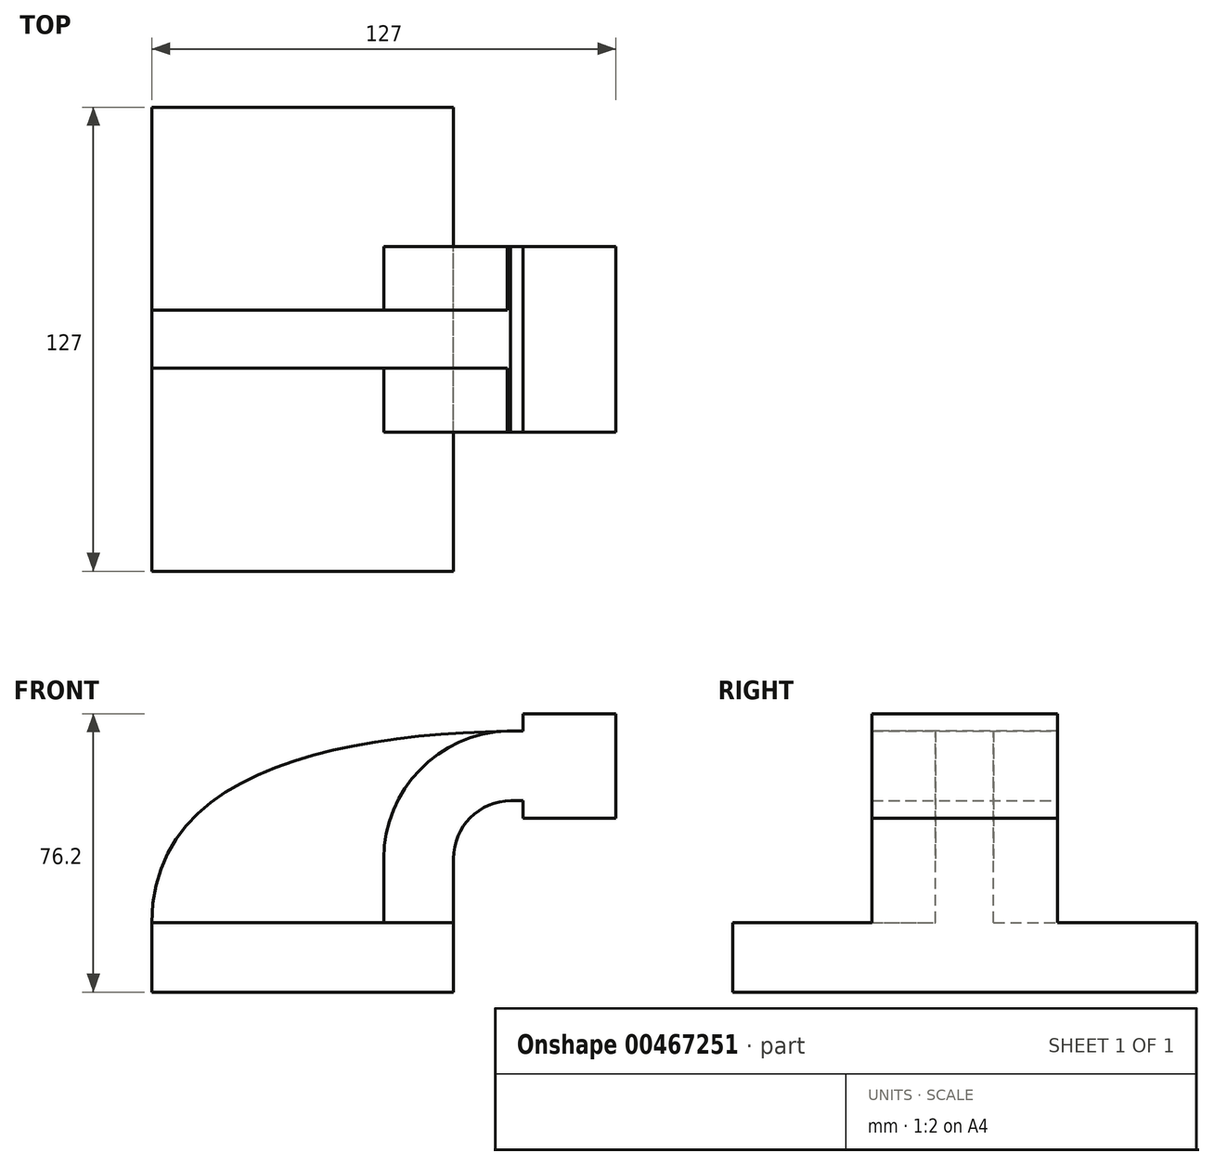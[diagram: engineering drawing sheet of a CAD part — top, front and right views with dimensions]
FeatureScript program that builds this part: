
annotation { "Feature Type Name" : "Feature", "Feature Type Description" : "" }
export const myFeature = defineFeature(function(context is Context, id is Id, definition is map)
    precondition{}
    {
        {
            var Q0;
            Q0=qCreatedBy(makeId("Front.planeOp"),FACE);
            var sketch = newSketch(context, id + "F0", { "sketchPlane" : qUnion([Q0])});
            skLineSegment(sketch, "E0.bottom", {"start": v(41.27, 9.53) * mm, "end": v(-41.28, 9.53) * mm});
            skLineSegment(sketch, "E0.top", {"start": v(41.28, -9.52) * mm, "end": v(-41.27, -9.53) * mm});
            skLineSegment(sketch, "E0.left", {"start": v(41.28, 9.53) * mm, "end": v(41.28, -9.52) * mm});
            skLineSegment(sketch, "E0.right", {"start": v(-41.28, 9.53) * mm, "end": v(-41.27, -9.52) * mm});
            skPoint(sketch, "E0.middle", {"position": v(0, 0) * mm});
            skLineSegment(sketch, "E1.bottom", {"start": v(111.13, 66.68) * mm, "end": v(60.33, 66.68) * mm});
            skLineSegment(sketch, "E1.top", {"start": v(111.13, 38.1) * mm, "end": v(60.33, 38.1) * mm});
            skLineSegment(sketch, "E1.left", {"start": v(111.13, 66.68) * mm, "end": v(111.13, 38.1) * mm});
            skLineSegment(sketch, "E1.right", {"start": v(60.32, 66.68) * mm, "end": v(60.33, 38.1) * mm});
            skPoint(sketch, "E1.middle", {"position": v(85.73, 52.39) * mm});
            skLineSegment(sketch, "E2", {"start": v(41.27, 9.53) * mm, "end": v(41.27, 27) * mm});
            skArc(sketch, "E3", {"start": v(41.28, 27) * mm, "mid": v(45.89, 38.19) * mm, "end": v(57.04, 42.88) * mm});
            skLineSegment(sketch, "E4", {"start": v(57.04, 42.88) * mm, "end": v(60.33, 42.88) * mm});
            skLineSegment(sketch, "E5", {"start": v(57.04, 42.88) * mm, "end": v(85.62, 43.07) * mm});
            skLineSegment(sketch, "E6.0", {"start": v(56.91, 61.92) * mm, "end": v(85.5, 62.12) * mm});
            skArc(sketch, "E6.1", {"start": v(22.23, 27) * mm, "mid": v(32.37, 51.61) * mm, "end": v(56.91, 61.92) * mm});
            skLineSegment(sketch, "E6.2", {"start": v(22.22, 9.53) * mm, "end": v(22.22, 27) * mm});
            skLineSegment(sketch, "E7", {"start": v(85.73, 38.1) * mm, "end": v(85.73, 66.68) * mm});
            skFitSpline(sketch, "E8", {"points": [v(-41.28, 9.53) * mm, v(56.91, 61.92) * mm], "startDerivative": vector(0.02, 125.3) * mm, "endDerivative": vector(139.57, 2.52) * mm});
            skSolve(sketch);
        }
        {
            var Q0;
            Q0=makeQuery(id+"F0.imprint","IMPRINT",FACE,{"disambiguationData":[TD([[makeQuery(id+"F0.imprint","IMPRINT",EDGE,{"derivedFrom":sQuery(id+"F0.wireOp",EDGE,"E0.top")}),-1.0]])]});
            extrude(context, id + "F1", {"entities" : qUnion([Q0]), "endBound" : BoundingType.SYMMETRIC, "depth" : 127 * mm});
        }
        {
            var Q0;
            {var subQ0=sQuery(id+"F0.wireOp",EDGE,"E2");Q0=makeQuery(id+"F0.imprint","IMPRINT",FACE,{"disambiguationData":[TD([[makeQuery(id+"F0.imprint","IMPRINT",EDGE,{"derivedFrom":subQ0}),1.0]])]});}
            var Q1;
            {var subQ6=sQuery(id+"F0.wireOp",EDGE,"E7");Q1=makeQuery(id+"F0.imprint","IMPRINT",FACE,{"disambiguationData":[TD([[makeQuery(id+"F0.imprint","IMPRINT",EDGE,{"derivedFrom":subQ6}),1.0]])]});}
            extrude(context, id + "F2", {"entities" : qUnion([Q0, Q1]), "operationType" : NewBodyOperationType.ADD, "endBound" : BoundingType.SYMMETRIC, "depth" : 50.8 * mm});
        }
        {
            var Q0;
            {var subQ3=sQuery(id+"F0.wireOp",EDGE,"E6.2");Q0=makeQuery(id+"F0.imprint","IMPRINT",FACE,{"disambiguationData":[TD([[makeQuery(id+"F0.imprint","IMPRINT",EDGE,{"derivedFrom":subQ3}),1.0]])]});}
            extrude(context, id + "F3", {"entities" : qUnion([Q0]), "operationType" : NewBodyOperationType.ADD, "endBound" : BoundingType.SYMMETRIC, "depth" : 15.88 * mm});
        }
    });
